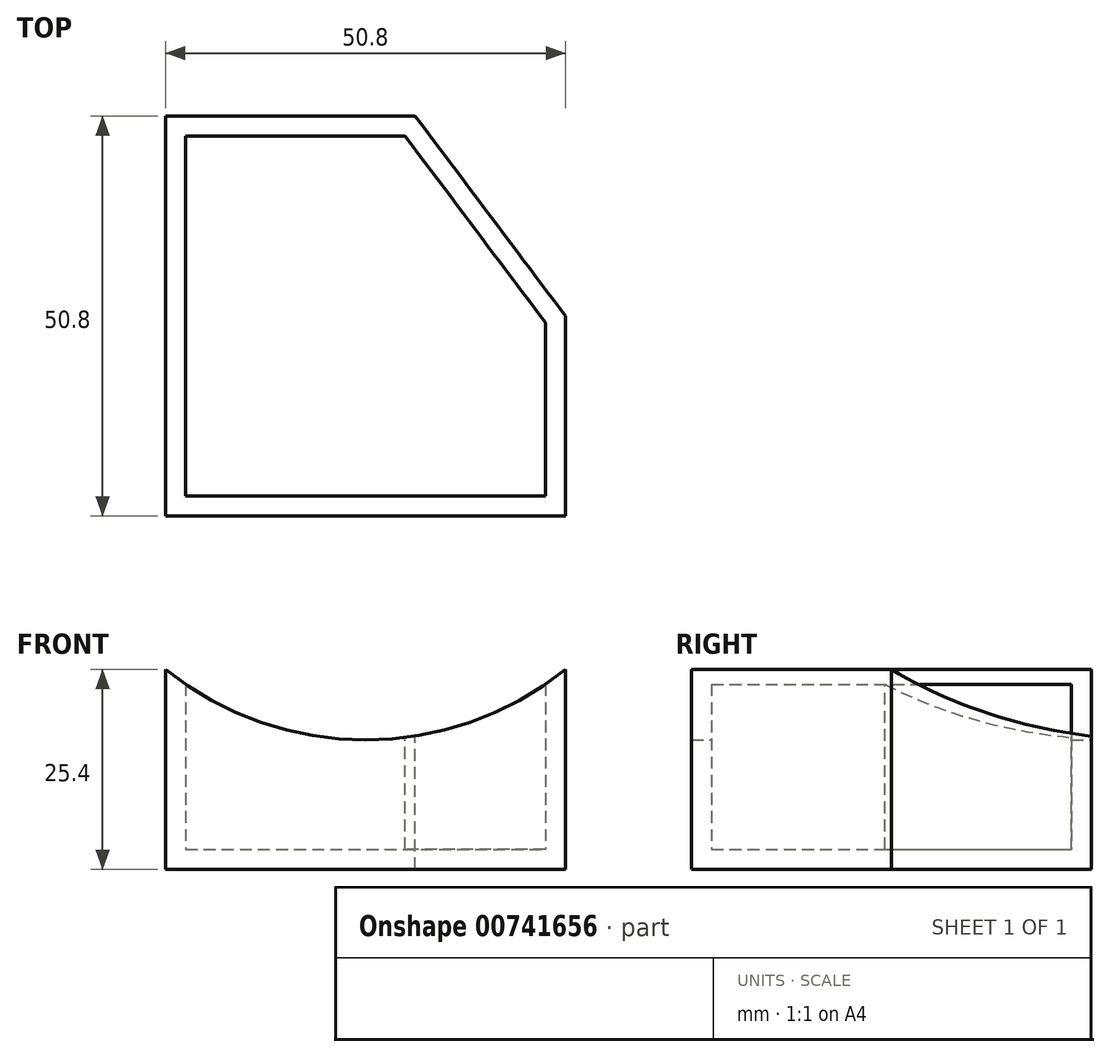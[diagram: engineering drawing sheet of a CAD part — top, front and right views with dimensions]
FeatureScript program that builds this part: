
annotation { "Feature Type Name" : "Feature", "Feature Type Description" : "" }
export const myFeature = defineFeature(function(context is Context, id is Id, definition is map)
    precondition{}
    {
        {
            var Q0;
            Q0=qCreatedBy(makeId("Front.planeOp"),FACE);
            var sketch = newSketch(context, id + "F0", { "sketchPlane" : qUnion([Q0])});
            skLineSegment(sketch, "E0.top", {"start": v(-31.71, -46.57) * mm, "end": v(19.09, -46.57) * mm});
            skLineSegment(sketch, "E0.left", {"start": v(-31.71, -21.17) * mm, "end": v(-31.71, -46.57) * mm});
            skLineSegment(sketch, "E0.right", {"start": v(19.09, -21.17) * mm, "end": v(19.09, -46.57) * mm});
            skArc(sketch, "E1", {"start": v(-31.71, -21.17) * mm, "mid": v(-6.31, -30.14) * mm, "end": v(19.09, -21.17) * mm});
            skSolve(sketch);
        }
        {
            var Q0;
            Q0=makeQuery(id+"F0.imprint","IMPRINT",FACE,{"disambiguationData":[TD([[makeQuery(id+"F0.imprint","IMPRINT",EDGE,{"derivedFrom":sQuery(id+"F0.wireOp",EDGE,"E0.top")}),1.0]])]});
            extrude(context, id + "F1", {"entities" : qUnion([Q0]), "depth" : 50.8 * mm, "offsetDistance" : 25.4 * mm});
        }
        {
            var Q0;
            Q0=qCreatedBy(makeId("Top.planeOp"),FACE);
            var sketch = newSketch(context, id + "F2", { "sketchPlane" : qUnion([Q0])});
            skLineSegment(sketch, "E2.0.0", {"start": v(19.09, 0) * mm, "end": v(-31.71, 0) * mm});
            skLineSegment(sketch, "E2.0.1", {"start": v(-31.71, 0) * mm, "end": v(-31.71, -50.8) * mm});
            skLineSegment(sketch, "E2.0.2", {"start": v(-31.71, -50.8) * mm, "end": v(19.09, -50.8) * mm});
            skLineSegment(sketch, "E2.0.3", {"start": v(19.09, -50.8) * mm, "end": v(19.09, 0) * mm});
            skLineSegment(sketch, "E3", {"start": v(19.09, -25.4) * mm, "end": v(2.3, -50.8) * mm});
            skLineSegment(sketch, "E4", {"start": v(2.3, -50.8) * mm, "end": v(19.09, -25.4) * mm});
            skLineSegment(sketch, "E5", {"start": v(19.09, -25.4) * mm, "end": v(0, 0) * mm});
            skSolve(sketch);
        }
        {
            var Q0;
            {var subQ3=sQuery(id+"F2.wireOp",EDGE,"E4");Q0=makeQuery(id+"F2.imprint","IMPRINT",FACE,{"disambiguationData":[TD([[makeQuery(id+"F2.imprint","IMPRINT",EDGE,{"derivedFrom":subQ3}),-1.0]])]});}
            var Q1;
            {var subQ3=sQuery(id+"F2.wireOp",EDGE,"E5");Q1=makeQuery(id+"F2.imprint","IMPRINT",FACE,{"disambiguationData":[TD([[makeQuery(id+"F2.imprint","IMPRINT",EDGE,{"derivedFrom":subQ3}),-1.0]])]});}
            extrude(context, id + "F3", {"entities" : qUnion([Q0, Q1]), "operationType" : NewBodyOperationType.REMOVE, "endBound" : BoundingType.THROUGH_ALL, "oppositeDirection" : true, "depth" : 25.4 * mm, "offsetDistance" : 25.4 * mm});
        }
        {
            var Q0;
            Q0=makeQuery(id+"F1.opExtrude","SWEPT_FACE",FACE,{"disambiguationData":[OSD([sQuery(id+"F0.wireOp",EDGE,"E1")])]});
            shell(context, id + "F4", {"entities" : qUnion([Q0]), "thickness" : 2.54 * mm});
        }
    });
